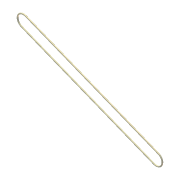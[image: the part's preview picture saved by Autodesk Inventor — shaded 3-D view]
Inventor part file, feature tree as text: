
AUTODESK INVENTOR PART (.ipt)
format: ipt  version: 2012 (Build 160160000, 160)  size: 93,184 bytes
history: native  units: in
note: dims shown in document units (in); Inventor stores cm internally (conversion verified against a paired STEP export)
features: extrude x1, fillet x1, sketch x1
ambient origin geometry x8: Origin, YZ Plane, XZ Plane, XY Plane, X Axis, Y Axis, Z Axis, Center Point
bodies: Solid1 (feature_tree)
feature tree (3):
  extrude  "Extrusion1"  Depth=0.1875in
  fillet  "Fillet1"  Radius=0.1875in
  sketch  "Sketch1"  dims[d0=1.0in d1=0.1875in d2=0.1875in d3=0.0in d4=0.1875in d5=0.0938in]
